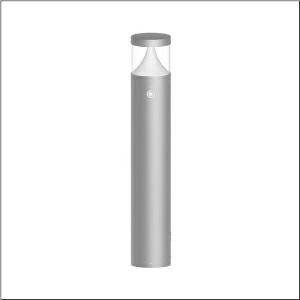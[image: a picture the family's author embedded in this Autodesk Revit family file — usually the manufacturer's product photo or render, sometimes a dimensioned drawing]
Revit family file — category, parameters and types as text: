
# Revit family: cl_31_poller_90_sensor_5cl444803
name_source: partatom
category: Lighting Fixtures
units: mm (PartAtom-declared; Revit-internal decimal feet)

## family parameters
Cut with Voids When Loaded = No
Host = Face
Light Source = No
Part Type = Normal
Room Calculation Point = No
Round Connector Dimension = Use Diameter
Shared = No

## types (1)
- --- (1 x LED, 1500 lm, 14 W, 3000K)
    Apparent Load = 14 VA
    CIE Flux Codes = 19 66 88 92 100
    Color Rendering = 80
    Color Temperature = 3000K
    Default Elevation = 1800 mm
    Description = CL 31 Bollard 90 Sensor, bollard luminaire, primary light control with lens, of PC, primary optical cover: cover panel, of PC, transparent, secondary light control with reflector, of PC, primary light characteristic: asymmetric, LED, rated luminous flux: 1.500lm, luminous efficacy: 107lm/W, light colour: 830, colour temperature: 3000K, control gear: ECG DALI, with terminal, 5-pole, max. 2.5mm², mains connection: 220..240V, AC, 50/60Hz, rated input power: 14W, luminaire housing, of aluminium, powder-coated, Siteco® metallic grey, diameter: 170mm, height: 900mm, PIR sensor, protection rating (complete): IP65, insulation class (complete): insulation class I (protective earthing), certification: CE, ENEC, impact resistance: IK08, permissible operating ambient temperature for outdoor applications: -20..+50°C, packaging unit: 1 piece
    Height = 200 mm  [stored 0.656168 ft]
    Lamp = 1 x LED
    Lamp Light Flux = 1500 lm
    Lamp Power = 14 W
    Lamp count = 1
    Length = 170 mm  [stored 0.557743 ft]
    Luminous efficacy = 107 lm/W
    Manufacturer = Siteco
    ModVariant = No
    Model = 5CL444803
    Mounting Place = Floor
    Mounting Type = Freestanding
    Number of Poles = 1
    OnlyDefault = Yes
    Power Factor = 1
    Product Name = CL 31 Poller 90 Sensor
    Product group = bollard luminaire
    ProductGroupID = 1304
    Protection Class = Protection class I
    Protection Degree = IP 65
    RLX_Detail_Level = 1
    RLX_Emergency_Light_Flux = 0 lm
    RLX_Emergency_Type = 0
    RLX_Emergency_Type_DB = No
    RlxData = <blob elided: 65729 chars, md5=82fd7028>
    Socket = socket
    Standby Power = 0 W
    System Light Flux = 1500 lm
    System Power = 14 W
    Type Comments = factory setting: luminous flux: 100 % | dim-lin: 254 | 350 mA
    Type Image = l_1006897.jpg
    URL = http://relux.com
    VarID = @adj_167809
    Voltage = 0 V
    Weight = 0.00 kg
    Width = 0 mm  [stored 0 ft]

note: [stored X ft] marks values corroborated as IEEE doubles in the binary element streams (Revit-internal decimal feet)

## geometry (parser evidence)
native form markers: Blend x4, Sweep x10
no freeform markers — native parametric forms only
